# Revit family: Sanitary_Taps-Mixers_AXOR_48060XXX-AXOR-One-2-hole-basin-mixer-Sel_NEW
name_source: partatom
category: Plumbing Fixtures
revit_build: Autodesk Revit 2018 (Build: 20170223_1515(x64)
units: mm (PartAtom-declared; Revit-internal decimal feet)

## family parameters
Always vertical = No
Cut with Voids When Loaded = No
OmniClass Number = 23.31.11.00
OmniClass Title = Faucets
Part Type = Normal
Room Calculation Point = No
Round Connector Dimension = Use Diameter
Shared = No
Work Plane-Based = Yes

## types (1)
- Default - please load Revit Family Type Catalog
    Always visible = Yes
    BIMobject category = Taps & Mixers
    Connector Description = Water Inlet 9.5 mm
    Date of publishing = 9/28/2022 12:00:00 AM
    Default Elevation = 1219.2 mm
    Description = AXOR One 2-hole basin mixer Select 260 with push-open waste set
    Design country = Germany
    Diameter = 10 mm
    EAN code = 4059625469781
    Edition number = 1
    GTIN code = https://4059625469781
    IFC Classification = Valve
    Manufacturer = AXOR
    Manufacturer country = Germany
    Manufacturer name = AXOR
    Masterformat 2014 Code = 22 41 39
    Masterformat 2014 Description = Residential Faucets, Supplies, and Trim
    Material 1 = AXOR - Metal - 000 Chrome
    Model = 48060XXX
    OmniClass Code = 23-31 11 00
    OmniClass Description = Faucets
    Product Guid = 2facab20-23a9-4622-8487-19261b867d8b
    Product SKU = 48060XXX
    Product data url = https://bimobject.com
    Product family = AXOR One
    Product group = Basin mixers
    Product name = 48060XXX AXOR One 2-hole basin mixer Select 260 with push-open waste set
    Product url = https://www.axor-design.com
    QR code = https://bimobject.com
    UNSPSC Code = 301815
    URL = https://www.axor-design.com
    Uniclass 2015 Code = Pr_40_20_87
    Uniclass 2015 Name = Taps and water supply outlet fittings
    Uniformat II Code = D2010
    Uniformat II Description = Plumbing Fixtures
    Weight Net (Kg) = 2.6

## geometry (parser evidence)
native form markers: Sweep x1
no freeform markers — native parametric forms only
